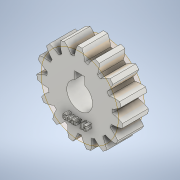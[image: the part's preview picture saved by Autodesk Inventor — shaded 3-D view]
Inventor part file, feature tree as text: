
AUTODESK INVENTOR PART (.ipt)
format: ipt  version: 2021 (Build 250183000, 183)  size: 439,808 bytes
history: native  units: mm (DEFAULTED — no unit token found)
features: sketch x4, plane x3, other x3, extrude x2, emboss x1
ambient origin geometry x8: Origin, YZ Plane, XZ Plane, XY Plane, X Axis, Y Axis, Z Axis, Center Point
bodies: Solid1 (feature_tree)
feature tree (13):
  extrude  "Extrusion1"  Depth=5.0mm TaperAngle=0.0deg
  plane  "Work Plane2"
  plane  "Work Plane8"
  plane  "Work Plane9"
  other  "Spur Gear"
  extrude  "Extrusion2"  Depth=10.0mm TaperAngle=0.0deg
  emboss  "Emboss1"
  sketch  "Sketch1"  dims[d0=16.6mm d1=5.0mm d2=0.0mm]
  sketch  "Sketch2"  dims[d3=15.0mm d4=10.0mm d5=0.0mm]
  other  "Srf1"
  sketch  "Sketch4"  dims[d16=22.5mm]
  sketch  "Sketch5"  dims[d17=0.0mm d34=2.094395mm d39=0.0mm d41=0.0mm d43=22.5mm d46=22.5mm d47=0.0mm d48=0.0mm d57=5.0mm d58=2.0mm d59=1.5mm d60=5.0mm d61=0.0mm d62=1.0mm d63=0.0mm]
  other  "Pitch Diameter"
